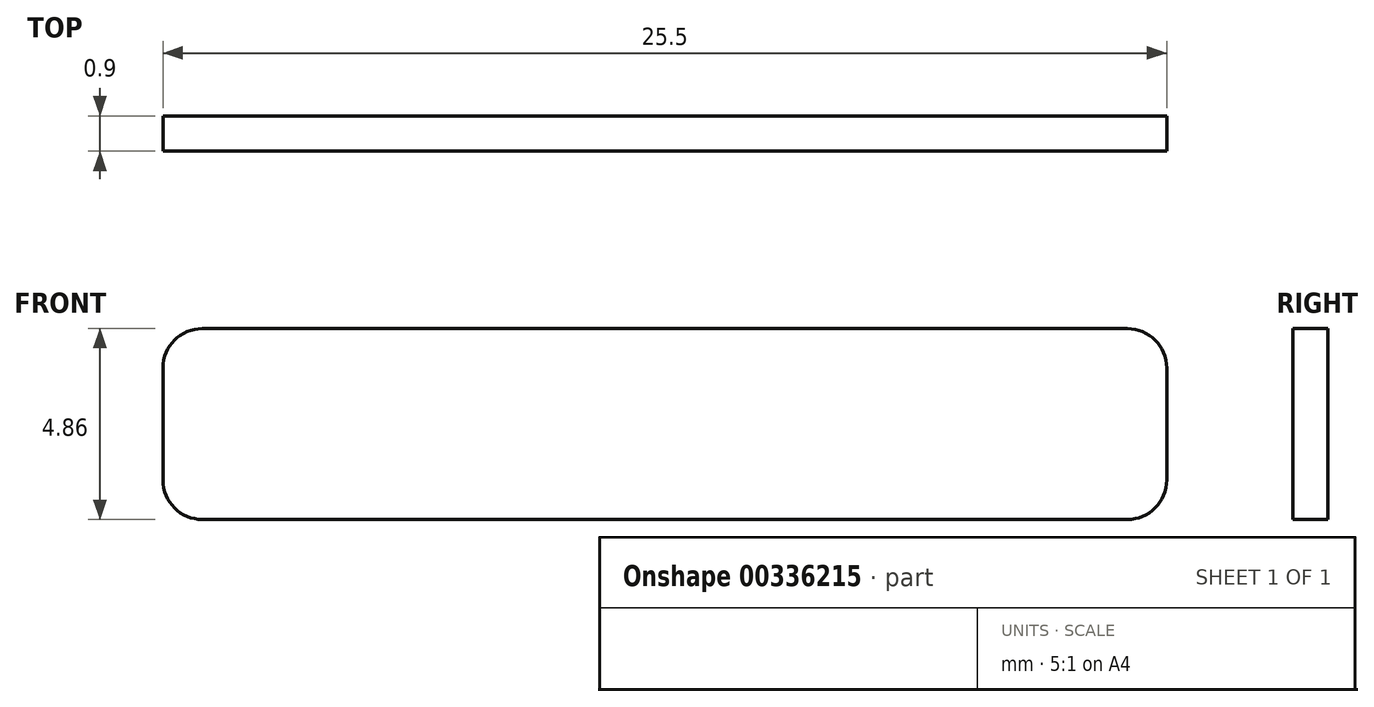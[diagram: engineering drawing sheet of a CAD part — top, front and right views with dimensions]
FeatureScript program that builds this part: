
annotation { "Feature Type Name" : "Feature", "Feature Type Description" : "" }
export const myFeature = defineFeature(function(context is Context, id is Id, definition is map)
    precondition{}
    {
        {
            var Q0;
            Q0=qCreatedBy(makeId("Front.planeOp"),FACE);
            var sketch = newSketch(context, id + "F0", { "sketchPlane" : qUnion([Q0])});
            skLineSegment(sketch, "E0.bottom", {"start": v(12.75, 2.43) * mm, "end": v(-12.75, 2.43) * mm});
            skLineSegment(sketch, "E0.top", {"start": v(12.75, -2.43) * mm, "end": v(-12.75, -2.43) * mm});
            skLineSegment(sketch, "E0.left", {"start": v(12.75, 2.43) * mm, "end": v(12.75, -2.43) * mm});
            skLineSegment(sketch, "E0.right", {"start": v(-12.75, 2.43) * mm, "end": v(-12.75, -2.43) * mm});
            skPoint(sketch, "E0.middle", {"position": v(0, 0) * mm});
            skSolve(sketch);
        }
        {
            var Q0;
            Q0=makeQuery(id+"F0.imprint","IMPRINT",FACE,{"disambiguationData":[TD([[makeQuery(id+"F0.imprint","IMPRINT",EDGE,{"derivedFrom":sQuery(id+"F0.wireOp",EDGE,"E0.bottom")}),1.0]])]});
            extrude(context, id + "F1", {"entities" : qUnion([Q0]), "depth" : 0.9 * mm});
        }
        {
            var Q0;
            Q0=makeQuery(id+"F1.opExtrude","SWEPT_EDGE",EDGE,{"disambiguationData":[OSD([sQuery(id+"F0.wireOp",EDGE,"E0.bottom"),sQuery(id+"F0.wireOp",EDGE,"E0.left")])]});
            var Q1;
            Q1=makeQuery(id+"F1.opExtrude","SWEPT_EDGE",EDGE,{"disambiguationData":[OSD([sQuery(id+"F0.wireOp",EDGE,"E0.top"),sQuery(id+"F0.wireOp",EDGE,"E0.left")])]});
            var Q2;
            Q2=makeQuery(id+"F1.opExtrude","SWEPT_EDGE",EDGE,{"disambiguationData":[OSD([sQuery(id+"F0.wireOp",EDGE,"E0.bottom"),sQuery(id+"F0.wireOp",EDGE,"E0.right")])]});
            var Q3;
            Q3=makeQuery(id+"F1.opExtrude","SWEPT_EDGE",EDGE,{"disambiguationData":[OSD([sQuery(id+"F0.wireOp",EDGE,"E0.top"),sQuery(id+"F0.wireOp",EDGE,"E0.right")])]});
            fillet(context, id + "F2", {"entities" : qUnion([Q0, Q1, Q2, Q3]), "radius" : 1 * mm, "tangentPropagation" : true, "allowEdgeOverflow" : false});
        }
    });
